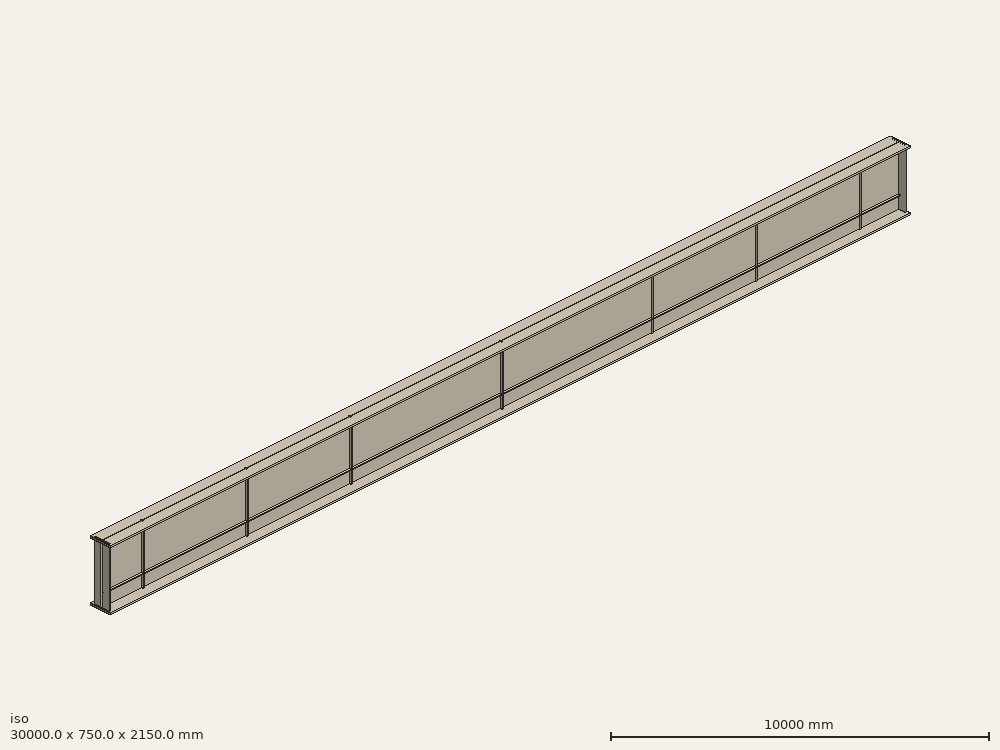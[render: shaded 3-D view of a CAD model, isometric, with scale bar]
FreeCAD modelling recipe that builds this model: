
FCSTD DOCUMENT  (FreeCAD 0.21R33694 (Git))
Label: Plate_girder_EC3
License: All rights reserved
LicenseURL: http://en.wikipedia.org/wiki/All_rights_reserved
objects: Sketcher::SketchObject×13, Part::Extrusion×13, Fem::ConstraintForce×5, Part::FeaturePython×2, Fem::ConstraintDisplacement×2, Fem::FemSolverObjectPython×1, App::MaterialObjectPython×1, Fem::FemAnalysis×1, Fem::FemMeshObjectPython×1
note: 28 computed .brp shape members not serialized (recipe doc carries the construction recipe); baked Part::Feature solids carry a one-line shape summary decoded from their .brp

FEATURE [Fem::FemSolverObjectPython] SolverCcxTools  # FEM object (typed FeaturePython)
  AnalysisType = 0
  BeamShellResultOutput3D = false
  BucklingFactors = 1
  EigenmodeHighLimit = 1000000
  EigenmodeLowLimit = 0
  EigenmodesCount = 10
  GeometricalNonlinearity = 0
  IterationsControlParameterCutb = 0.25,0.5,0.75,0.85,,,1.5,
  IterationsControlParameterIter = 4,8,9,200,10,400,,200,,
  IterationsControlParameterTimeUse = false
  IterationsThermoMechMaximum = 2000
  IterationsUserDefinedIncrementations = false
  IterationsUserDefinedTimeStepLength = false
  MaterialNonlinearity = 0
  MatrixSolverType = 0
  SplitInputWriter = false
  ThermoMechSteadyState = true
  TimeEnd = 1
  TimeInitialStep = 0.01
FEATURE [App::MaterialObjectPython] MaterialSolid  # material (typed FeaturePython)
  Category = 0
  Material = AuthorAndLicense=(c) 2014 M. Münch - GNU Lesser General Public License (LGPL),CardName=Steel-St-E-315,Density=7800 kg/m^3,Father=Metal,+13 more (map truncated)
FEATURE [Sketcher::SketchObject] Sketch001  label="end stiffener"
  FullyConstrained = true
  Placement = pos=(0,0,0) rot=(0.57735,0.57735,0.57735;2.0944rad)
  sketch-geometry (4):
    g0: LineSegment StartX=87.5 StartY=2100 StartZ=0 EndX=662.5 EndY=2100 EndZ=0
    g1: LineSegment StartX=662.5 StartY=2100 StartZ=0 EndX=662.5 EndY=0 EndZ=0
    g2: LineSegment StartX=662.5 StartY=0 StartZ=0 EndX=87.5 EndY=0 EndZ=0
    g3: LineSegment StartX=87.5 StartY=0 StartZ=0 EndX=87.5 EndY=2100 EndZ=0
  constraints (12):
    c: Coincident(g0,g1)
    c: Coincident(g1,g2)
    c: Coincident(g2,g3)
    c: Coincident(g3,g0)
    c: Horizontal(g0)
    c: Horizontal(g2)
    c: Vertical(g1)
    c: Vertical(g3)
    c: DistanceY(g1,g1) = 2100
    c: PointOnObject(g2,g-1)
    c: DistanceX(g2,g2) = 575
    c: DistanceX(g-1,g2) = 87.5
FEATURE [Sketcher::SketchObject] Sketch002  label="stiffener"
  FullyConstrained = true
  Placement = pos=(0,0,0) rot=(0.57735,0.57735,0.57735;2.0944rad)
  sketch-geometry (4):
    g0: LineSegment StartX=287.5 StartY=2100 StartZ=0 EndX=462.5 EndY=2100 EndZ=0
    g1: LineSegment StartX=462.5 StartY=2100 StartZ=0 EndX=462.5 EndY=0 EndZ=0
    g2: LineSegment StartX=462.5 StartY=0 StartZ=0 EndX=287.5 EndY=0 EndZ=0
    g3: LineSegment StartX=287.5 StartY=0 StartZ=0 EndX=287.5 EndY=2100 EndZ=0
  constraints (12):
    c: Coincident(g0,g1)
    c: Coincident(g1,g2)
    c: Coincident(g2,g3)
    c: Coincident(g3,g0)
    c: Horizontal(g0)
    c: Horizontal(g2)
    c: Vertical(g1)
    c: Vertical(g3)
    c: DistanceY(g1,g1) = 2100
    c: PointOnObject(g2,g-1)
    c: DistanceX(g0,g0) = 175
    c: DistanceX(g-1,g2) = 287.5
FEATURE [Sketcher::SketchObject] Sketch003
  FullyConstrained = true
  sketch-geometry (4):
    g0: LineSegment StartX=0 StartY=462.5 StartZ=0 EndX=175 EndY=462.5 EndZ=0
    g1: LineSegment StartX=175 StartY=462.5 StartZ=0 EndX=175 EndY=287.5 EndZ=0
    g2: LineSegment StartX=175 StartY=287.5 StartZ=0 EndX=0 EndY=287.5 EndZ=0
    g3: LineSegment StartX=0 StartY=287.5 StartZ=0 EndX=0 EndY=462.5 EndZ=0
  constraints (12):
    c: Coincident(g0,g1)
    c: Coincident(g1,g2)
    c: Coincident(g2,g3)
    c: Coincident(g3,g0)
    c: Horizontal(g0)
    c: Horizontal(g2)
    c: Vertical(g1)
    c: Vertical(g3)
    c: DistanceX(g0,g0) = 175
    c: DistanceY(g1,g1) = 175
    c: PointOnObject(g2,g-2)
    c: DistanceY(g-1,g2) = 287.5
FEATURE [Part::Extrusion] Extrude001  label="load pad"
  Base = -> Sketch003
  Dir = (0,0,1)
  DirMode = 2
  FaceMakerClass = Part::FaceMakerBullseye
  LengthFwd = 0
  LengthRev = 50
  Placement = pos=(9262.5,0,0) rot=(0,0,1;0rad)
  Solid = true
  Symmetric = false
FEATURE [Part::Extrusion] Extrude002  label="stiffener001"
  Base = -> Sketch002
  Dir = (1,0,0)
  DirMode = 2
  FaceMakerClass = Part::FaceMakerBullseye
  LengthFwd = 15
  LengthRev = 0
  Placement = pos=(1542.5,0,0) rot=(0,0,1;0rad)
  Solid = true
  Symmetric = false
FEATURE [Part::Extrusion] Extrude003  label="end stiffener001"
  Base = -> Sketch001
  Dir = (1,0,0)
  DirMode = 2
  FaceMakerClass = Part::FaceMakerBullseye
  LengthFwd = 24
  LengthRev = 0
  Placement = pos=(50,0,0) rot=(0,0,1;0rad)
  Solid = true
  Symmetric = false
FEATURE [Sketcher::SketchObject] Sketch004  label="end stiffener003"
  FullyConstrained = true
  Placement = pos=(0,0,0) rot=(0.57735,0.57735,0.57735;2.0944rad)
  sketch-geometry (4):
    g0: LineSegment StartX=87.5 StartY=2100 StartZ=0 EndX=662.5 EndY=2100 EndZ=0
    g1: LineSegment StartX=662.5 StartY=2100 StartZ=0 EndX=662.5 EndY=0 EndZ=0
    g2: LineSegment StartX=662.5 StartY=0 StartZ=0 EndX=87.5 EndY=0 EndZ=0
    g3: LineSegment StartX=87.5 StartY=0 StartZ=0 EndX=87.5 EndY=2100 EndZ=0
  constraints (12):
    c: Coincident(g0,g1)
    c: Coincident(g1,g2)
    c: Coincident(g2,g3)
    c: Coincident(g3,g0)
    c: Horizontal(g0)
    c: Horizontal(g2)
    c: Vertical(g1)
    c: Vertical(g3)
    c: DistanceY(g1,g1) = 2100
    c: PointOnObject(g2,g-1)
    c: DistanceX(g2,g2) = 575
    c: DistanceX(g-1,g2) = 87.5
FEATURE [Part::Extrusion] Extrude004  label="end stiffener002"
  Base = -> Sketch004
  Dir = (1,0,0)
  DirMode = 2
  FaceMakerClass = Part::FaceMakerBullseye
  LengthFwd = 24
  LengthRev = 0
  Placement = pos=(29926,0,0) rot=(0,0,1;0rad)
  Solid = true
  Symmetric = false
FEATURE [Sketcher::SketchObject] Sketch005  label="stiffener003"
  FullyConstrained = true
  Placement = pos=(0,0,0) rot=(0.57735,0.57735,0.57735;2.0944rad)
  sketch-geometry (4):
    g0: LineSegment StartX=287.5 StartY=2100 StartZ=0 EndX=462.5 EndY=2100 EndZ=0
    g1: LineSegment StartX=462.5 StartY=2100 StartZ=0 EndX=462.5 EndY=0 EndZ=0
    g2: LineSegment StartX=462.5 StartY=0 StartZ=0 EndX=287.5 EndY=0 EndZ=0
    g3: LineSegment StartX=287.5 StartY=0 StartZ=0 EndX=287.5 EndY=2100 EndZ=0
  constraints (12):
    c: Coincident(g0,g1)
    c: Coincident(g1,g2)
    c: Coincident(g2,g3)
    c: Coincident(g3,g0)
    c: Horizontal(g0)
    c: Horizontal(g2)
    c: Vertical(g1)
    c: Vertical(g3)
    c: DistanceY(g1,g1) = 2100
    c: PointOnObject(g2,g-1)
    c: DistanceX(g0,g0) = 175
    c: DistanceX(g-1,g2) = 287.5
FEATURE [Part::Extrusion] Extrude005  label="stiffener002"
  Base = -> Sketch005
  Dir = (1,0,0)
  DirMode = 2
  FaceMakerClass = Part::FaceMakerBullseye
  LengthFwd = 15
  LengthRev = 0
  Placement = pos=(5442.5,0,0) rot=(0,0,1;0rad)
  Solid = true
  Symmetric = false
FEATURE [Sketcher::SketchObject] Sketch006  label="stiffener005"
  FullyConstrained = true
  Placement = pos=(0,0,0) rot=(0.57735,0.57735,0.57735;2.0944rad)
  sketch-geometry (4):
    g0: LineSegment StartX=287.5 StartY=2100 StartZ=0 EndX=462.5 EndY=2100 EndZ=0
    g1: LineSegment StartX=462.5 StartY=2100 StartZ=0 EndX=462.5 EndY=0 EndZ=0
    g2: LineSegment StartX=462.5 StartY=0 StartZ=0 EndX=287.5 EndY=0 EndZ=0
    g3: LineSegment StartX=287.5 StartY=0 StartZ=0 EndX=287.5 EndY=2100 EndZ=0
  constraints (12):
    c: Coincident(g0,g1)
    c: Coincident(g1,g2)
    c: Coincident(g2,g3)
    c: Coincident(g3,g0)
    c: Horizontal(g0)
    c: Horizontal(g2)
    c: Vertical(g1)
    c: Vertical(g3)
    c: DistanceY(g1,g1) = 2100
    c: PointOnObject(g2,g-1)
    c: DistanceX(g0,g0) = 175
    c: DistanceX(g-1,g2) = 287.5
FEATURE [Part::Extrusion] Extrude006  label="stiffener004"
  Base = -> Sketch006
  Dir = (1,0,0)
  DirMode = 2
  FaceMakerClass = Part::FaceMakerBullseye
  LengthFwd = 15
  LengthRev = 0
  Placement = pos=(9342.5,0,0) rot=(0,0,1;0rad)
  Solid = true
  Symmetric = false
FEATURE [Sketcher::SketchObject] Sketch007  label="stiffener007"
  FullyConstrained = true
  Placement = pos=(0,0,0) rot=(0.57735,0.57735,0.57735;2.0944rad)
  sketch-geometry (4):
    g0: LineSegment StartX=287.5 StartY=2100 StartZ=0 EndX=462.5 EndY=2100 EndZ=0
    g1: LineSegment StartX=462.5 StartY=2100 StartZ=0 EndX=462.5 EndY=0 EndZ=0
    g2: LineSegment StartX=462.5 StartY=0 StartZ=0 EndX=287.5 EndY=0 EndZ=0
    g3: LineSegment StartX=287.5 StartY=0 StartZ=0 EndX=287.5 EndY=2100 EndZ=0
  constraints (12):
    c: Coincident(g0,g1)
    c: Coincident(g1,g2)
    c: Coincident(g2,g3)
    c: Coincident(g3,g0)
    c: Horizontal(g0)
    c: Horizontal(g2)
    c: Vertical(g1)
    c: Vertical(g3)
    c: DistanceY(g1,g1) = 2100
    c: PointOnObject(g2,g-1)
    c: DistanceX(g0,g0) = 175
    c: DistanceX(g-1,g2) = 287.5
FEATURE [Part::Extrusion] Extrude007  label="stiffener006"
  Base = -> Sketch007
  Dir = (1,0,0)
  DirMode = 2
  FaceMakerClass = Part::FaceMakerBullseye
  LengthFwd = 15
  LengthRev = 0
  Placement = pos=(14992.5,0,0) rot=(0,0,1;0rad)
  Solid = true
  Symmetric = false
FEATURE [Sketcher::SketchObject] Sketch008  label="stiffener009"
  FullyConstrained = true
  Placement = pos=(0,0,0) rot=(0.57735,0.57735,0.57735;2.0944rad)
  sketch-geometry (4):
    g0: LineSegment StartX=287.5 StartY=2100 StartZ=0 EndX=462.5 EndY=2100 EndZ=0
    g1: LineSegment StartX=462.5 StartY=2100 StartZ=0 EndX=462.5 EndY=0 EndZ=0
    g2: LineSegment StartX=462.5 StartY=0 StartZ=0 EndX=287.5 EndY=0 EndZ=0
    g3: LineSegment StartX=287.5 StartY=0 StartZ=0 EndX=287.5 EndY=2100 EndZ=0
  constraints (12):
    c: Coincident(g0,g1)
    c: Coincident(g1,g2)
    c: Coincident(g2,g3)
    c: Coincident(g3,g0)
    c: Horizontal(g0)
    c: Horizontal(g2)
    c: Vertical(g1)
    c: Vertical(g3)
    c: DistanceY(g1,g1) = 2100
    c: PointOnObject(g2,g-1)
    c: DistanceX(g0,g0) = 175
    c: DistanceX(g-1,g2) = 287.5
FEATURE [Part::Extrusion] Extrude008  label="stiffener008"
  Base = -> Sketch008
  Dir = (1,0,0)
  DirMode = 2
  FaceMakerClass = Part::FaceMakerBullseye
  LengthFwd = 15
  LengthRev = 0
  Placement = pos=(20642.5,0,0) rot=(0,0,1;0rad)
  Solid = true
  Symmetric = false
FEATURE [Sketcher::SketchObject] Sketch009  label="stiffener011"
  FullyConstrained = true
  Placement = pos=(0,0,0) rot=(0.57735,0.57735,0.57735;2.0944rad)
  sketch-geometry (4):
    g0: LineSegment StartX=287.5 StartY=2100 StartZ=0 EndX=462.5 EndY=2100 EndZ=0
    g1: LineSegment StartX=462.5 StartY=2100 StartZ=0 EndX=462.5 EndY=0 EndZ=0
    g2: LineSegment StartX=462.5 StartY=0 StartZ=0 EndX=287.5 EndY=0 EndZ=0
    g3: LineSegment StartX=287.5 StartY=0 StartZ=0 EndX=287.5 EndY=2100 EndZ=0
  constraints (12):
    c: Coincident(g0,g1)
    c: Coincident(g1,g2)
    c: Coincident(g2,g3)
    c: Coincident(g3,g0)
    c: Horizontal(g0)
    c: Horizontal(g2)
    c: Vertical(g1)
    c: Vertical(g3)
    c: DistanceY(g1,g1) = 2100
    c: PointOnObject(g2,g-1)
    c: DistanceX(g0,g0) = 175
    c: DistanceX(g-1,g2) = 287.5
FEATURE [Part::Extrusion] Extrude009  label="stiffener010"
  Base = -> Sketch009
  Dir = (1,0,0)
  DirMode = 2
  FaceMakerClass = Part::FaceMakerBullseye
  LengthFwd = 15
  LengthRev = 0
  Placement = pos=(24542.5,0,0) rot=(0,0,1;0rad)
  Solid = true
  Symmetric = false
FEATURE [Sketcher::SketchObject] Sketch010  label="stiffener013"
  FullyConstrained = true
  Placement = pos=(0,0,0) rot=(0.57735,0.57735,0.57735;2.0944rad)
  sketch-geometry (4):
    g0: LineSegment StartX=287.5 StartY=2100 StartZ=0 EndX=462.5 EndY=2100 EndZ=0
    g1: LineSegment StartX=462.5 StartY=2100 StartZ=0 EndX=462.5 EndY=0 EndZ=0
    g2: LineSegment StartX=462.5 StartY=0 StartZ=0 EndX=287.5 EndY=0 EndZ=0
    g3: LineSegment StartX=287.5 StartY=0 StartZ=0 EndX=287.5 EndY=2100 EndZ=0
  constraints (12):
    c: Coincident(g0,g1)
    c: Coincident(g1,g2)
    c: Coincident(g2,g3)
    c: Coincident(g3,g0)
    c: Horizontal(g0)
    c: Horizontal(g2)
    c: Vertical(g1)
    c: Vertical(g3)
    c: DistanceY(g1,g1) = 2100
    c: PointOnObject(g2,g-1)
    c: DistanceX(g0,g0) = 175
    c: DistanceX(g-1,g2) = 287.5
FEATURE [Part::Extrusion] Extrude010  label="stiffener012"
  Base = -> Sketch010
  Dir = (1,0,0)
  DirMode = 2
  FaceMakerClass = Part::FaceMakerBullseye
  LengthFwd = 15
  LengthRev = 0
  Placement = pos=(28442.5,0,0) rot=(0,0,1;0rad)
  Solid = true
  Symmetric = false
FEATURE [Sketcher::SketchObject] Sketch  label="girder"
  FullyConstrained = true
  Placement = pos=(0,0,0) rot=(0.57735,0.57735,0.57735;2.0944rad)
  sketch-geometry (16):
    g0: LineSegment StartX=750 StartY=2100 StartZ=0 EndX=750 EndY=2050 EndZ=0
    g1: LineSegment StartX=750 StartY=2050 StartZ=0 EndX=382.5 EndY=2050 EndZ=0
    g2: LineSegment StartX=382.5 StartY=2050 StartZ=0 EndX=382.5 EndY=50 EndZ=0
    g3: LineSegment StartX=382.5 StartY=50 StartZ=0 EndX=750 EndY=50 EndZ=0
    g4: LineSegment StartX=750 StartY=50 StartZ=0 EndX=750 EndY=0 EndZ=0
    g5: LineSegment StartX=0 StartY=0 StartZ=0 EndX=0 EndY=50 EndZ=0
    g6: LineSegment StartX=0 StartY=50 StartZ=0 EndX=367.5 EndY=50 EndZ=0
    g7: LineSegment StartX=367.5 StartY=50 StartZ=0 EndX=367.5 EndY=2050 EndZ=0
    g8: LineSegment StartX=367.5 StartY=2050 StartZ=0 EndX=0 EndY=2050 EndZ=0
    g9: LineSegment StartX=750 StartY=2100 StartZ=0 EndX=382.5 EndY=2100 EndZ=0
    g10: LineSegment StartX=750 StartY=0 StartZ=0 EndX=382.5 EndY=0 EndZ=0
    g11: LineSegment StartX=367.5 StartY=0 StartZ=0 EndX=0 EndY=0 EndZ=0
    g12: LineSegment StartX=382.5 StartY=2100 StartZ=0 EndX=367.5 EndY=2100 EndZ=0
    g13: LineSegment StartX=0 StartY=2050 StartZ=0 EndX=0 EndY=2100 EndZ=0
    g14: LineSegment StartX=367.5 StartY=0 StartZ=0 EndX=382.5 EndY=0 EndZ=0
    g15: LineSegment StartX=0 StartY=2100 StartZ=0 EndX=367.5 EndY=2100 EndZ=0
  constraints (48):
    c: Vertical(g0)
    c: Coincident(g0,g1)
    c: Horizontal(g1)
    c: Coincident(g1,g2)
    c: Vertical(g2)
    c: Coincident(g2,g3)
    c: Horizontal(g3)
    c: Coincident(g3,g4)
    c: PointOnObject(g4,g-1)
    c: Vertical(g5)
    c: Coincident(g5,g6)
    c: Horizontal(g6)
    c: Coincident(g6,g7)
    c: Vertical(g7)
    c: Coincident(g7,g8)
    c: Horizontal(g8)
    c: Vertical(g4)
    c: DistanceY(g0,g0) = 50
    c: DistanceX(g6,g6) = 367.5
    c: DistanceX(g3,g3) = 367.5
    c: DistanceY(g4,g4) = 50
    c: DistanceY(g5,g5) = 50
    c: DistanceY(g4,g0) = 2100
    c: DistanceX(g-1,g5) = 0
    c: Coincident(g9,g0)
    c: Horizontal(g9)
    c: Coincident(g10,g4)
    c: Horizontal(g10)
    c: Coincident(g11,g5)
    c: Horizontal(g11)
    c: Coincident(g12,g9)
    c: Horizontal(g12)
    c: Coincident(g13,g8)
    c: Vertical(g13)
    c: DistanceX(g7,g1) = 15
    c: Equal(g11,g6)
    c: Equal(g10,g3)
    c: Coincident(g14,g11)
    c: Coincident(g14,g10)
    c: DistanceY(g13,g13) = 50
    c: DistanceY(g-1,g5) = 0
    c: Coincident(g15,g13)
    c: Coincident(g15,g12)
    c: Horizontal(g15)
    c: DistanceX(g15,g15) = 367.5
    c: DistanceX(g12,g12) = 15
    c: DistanceX(g9,g9) = 367.5
    c: PointOnObject(g13,g-2)
FEATURE [Part::Extrusion] Extrude
  Base = -> Sketch
  Dir = (1,0,0)
  DirMode = 2
  FaceMakerClass = Part::FaceMakerBullseye
  LengthFwd = 30000
  LengthRev = 0
  Solid = true
  Symmetric = false
FEATURE [Sketcher::SketchObject] Sketch011
  FullyConstrained = true
  sketch-geometry (4):
    g0: LineSegment StartX=0 StartY=462.5 StartZ=0 EndX=175 EndY=462.5 EndZ=0
    g1: LineSegment StartX=175 StartY=462.5 StartZ=0 EndX=175 EndY=287.5 EndZ=0
    g2: LineSegment StartX=175 StartY=287.5 StartZ=0 EndX=0 EndY=287.5 EndZ=0
    g3: LineSegment StartX=0 StartY=287.5 StartZ=0 EndX=0 EndY=462.5 EndZ=0
  constraints (12):
    c: Coincident(g0,g1)
    c: Coincident(g1,g2)
    c: Coincident(g2,g3)
    c: Coincident(g3,g0)
    c: Horizontal(g0)
    c: Horizontal(g2)
    c: Vertical(g1)
    c: Vertical(g3)
    c: DistanceX(g0,g0) = 175
    c: DistanceY(g1,g1) = 175
    c: PointOnObject(g2,g-2)
    c: DistanceY(g-1,g2) = 287.5
FEATURE [Part::Extrusion] Extrude011  label="load pad001"
  Base = -> Sketch011
  Dir = (0,0,1)
  DirMode = 2
  FaceMakerClass = Part::FaceMakerBullseye
  LengthFwd = 0
  LengthRev = 50
  Placement = pos=(20562.5,0,0) rot=(0,0,1;0rad)
  Solid = true
  Symmetric = false
FEATURE [Part::FeaturePython] BooleanFragments  # WARN: FeaturePython — macro-defined, semantics opaque (R4)
  Mode = 2
  Objects = -> [Extrude001,Extrude002,Extrude003,Extrude004,Extrude005,Extrude006,Extrude007,Extrude008,Extrude009,Extrude010,Extrude,Extrude011]
  Tolerance = 0
FEATURE [Fem::ConstraintDisplacement] ConstraintDisplacement003
  NormalDirection = (0,0,1)
  Normals = (10) [(0,0,1),(0,0,1),(0,0,1),(0,0,1),(0,0,1),(0,0,1),(0,0,1),(0,0,1),(0,0,1),(0,0,1)]
  Points = (10) [(50,87.5,2100),(50,180.833,2100),(50,274.167,2100),(50,367.5,2100),(50,367.5,2100),(50,382.5,2100),(50,382.5,2100),(50,475.833,2100),+2 more]
  References = -> [BooleanFragments]
  Scale = 18
  hasXFormula = false
  hasYFormula = false
  hasZFormula = false
  rotxFix = false
  rotxFree = true
  rotyFix = false
  rotyFree = true
  rotzFix = false
  rotzFree = true
  useFlowSurfaceForce = false
  xDisplacement = 0
  xFix = false
  xFree = false
  xRotation = 0
  yDisplacement = 0
  yFix = false
  yFree = false
  yRotation = 0
  zDisplacement = 0
  zFix = false
  zFree = false
  zRotation = 0
FEATURE [Fem::ConstraintDisplacement] ConstraintDisplacement004
  NormalDirection = (0,0,1)
  Normals = (10) [(0,0,1),(0,0,1),(0,0,1),(0,0,1),(0,0,1),(0,0,1),(0,0,1),(0,0,1),(0,0,1),(0,0,1)]
  Points = (10) [(29950,87.5,2100),(29950,180.833,2100),(29950,274.167,2100),(29950,367.5,2100),(29950,367.5,2100),(29950,382.5,2100),(29950,382.5,2100),+3 more]
  References = -> [BooleanFragments]
  Scale = 18
  hasXFormula = false
  hasYFormula = false
  hasZFormula = false
  rotxFix = false
  rotxFree = true
  rotyFix = false
  rotyFree = true
  rotzFix = false
  rotzFree = true
  useFlowSurfaceForce = false
  xDisplacement = 0
  xFix = false
  xFree = true
  xRotation = 0
  yDisplacement = 0
  yFix = false
  yFree = false
  yRotation = 0
  zDisplacement = 0
  zFix = false
  zFree = false
  zRotation = 0
FEATURE [Fem::ConstraintForce] ConstraintForce005
  DirectionVector = (0,0,-1)
  Force = 2293000
  NormalDirection = (0,0,1)
  Points = (33) [(29950,87.5,2100),(29950,180.833,2100),(29950,274.167,2100),(29950,367.5,2100),(29938,87.5,2100),(29938,180.833,2100),(29938,274.167,2100),+26 more]
  References = -> [BooleanFragments]
  Reversed = true
  Scale = 13
FEATURE [Fem::ConstraintForce] ConstraintForce006
  DirectionVector = (0,0,-1)
  Force = 2293000
  NormalDirection = (0,0,1)
  Points = (33) [(74,87.5,2100),(74,180.833,2100),(74,274.167,2100),(74,367.5,2100),(62,87.5,2100),(62,180.833,2100),(62,274.167,2100),(62,367.5,2100),(50,87.5,2100),+24 more]
  References = -> [BooleanFragments]
  Reversed = true
  Scale = 13
FEATURE [Fem::ConstraintForce] ConstraintForce007
  DirectionVector = (0,0,1)
  Force = 925000
  NormalDirection = (0,0,-1)
  Points = (16) [(9262.5,287.5,-50),(9320.83,287.5,-50),(9379.17,287.5,-50),(9437.5,287.5,-50),(9262.5,345.833,-50),(9320.83,345.833,-50),(9379.17,345.833,-50),+9 more]
  References = -> [BooleanFragments]
  Reversed = true
  Scale = 14
FEATURE [Fem::ConstraintForce] ConstraintForce008
  DirectionVector = (0,0,1)
  Force = 925000
  NormalDirection = (0,0,-1)
  Points = (16) [(20562.5,287.5,-50),(20620.8,287.5,-50),(20679.2,287.5,-50),(20737.5,287.5,-50),(20562.5,345.833,-50),(20620.8,345.833,-50),(20679.2,345.833,-50),+9 more]
  References = -> [BooleanFragments]
  Reversed = true
  Scale = 14
FEATURE [Fem::ConstraintForce] ConstraintForce009
  DirectionVector = (0,0,1)
  Force = 2736000
  NormalDirection = (0,0,-1)
  Points = (323) [(29950,382.5,0),(29950,375,0),(29950,367.5,0),(29938,382.5,0),(29938,375,0),(29938,367.5,0),(29926,382.5,0),(29926,375,0),(29926,367.5,0),+314 more]
  References = -> [BooleanFragments]
  Reversed = true
FEATURE [Fem::FemAnalysis] Analysis
  Group = -> [SolverCcxTools,MaterialSolid,ConstraintDisplacement003,ConstraintDisplacement004,ConstraintForce005,ConstraintForce006,ConstraintForce007,ConstraintForce008,ConstraintForce009]
FEATURE [Sketcher::SketchObject] Sketch012
  FullyConstrained = true
  Placement = pos=(0,0,0) rot=(0.57735,0.57735,0.57735;2.0944rad)
  sketch-geometry (4):
    g0: LineSegment StartX=287.5 StartY=520 StartZ=0 EndX=462.5 EndY=520 EndZ=0
    g1: LineSegment StartX=462.5 StartY=520 StartZ=0 EndX=462.5 EndY=500 EndZ=0
    g2: LineSegment StartX=462.5 StartY=500 StartZ=0 EndX=287.5 EndY=500 EndZ=0
    g3: LineSegment StartX=287.5 StartY=500 StartZ=0 EndX=287.5 EndY=520 EndZ=0
  constraints (12):
    c: Coincident(g0,g1)
    c: Coincident(g1,g2)
    c: Coincident(g2,g3)
    c: Coincident(g3,g0)
    c: Horizontal(g0)
    c: Horizontal(g2)
    c: Vertical(g1)
    c: Vertical(g3)
    c: DistanceX(g2,g2) = 175
    c: DistanceY(g1,g1) = 20
    c: DistanceY(g-1,g2) = 500
    c: DistanceX(g-1,g2) = 287.5
FEATURE [Part::Extrusion] Extrude012
  Base = -> Sketch012
  Dir = (1,0,0)
  DirMode = 2
  FaceMakerClass = Part::FaceMakerBullseye
  LengthFwd = 29900
  LengthRev = 0
  Placement = pos=(50,0,0) rot=(0,0,1;0rad)
  Solid = true
  Symmetric = false
FEATURE [Part::FeaturePython] BooleanFragments001  # WARN: FeaturePython — macro-defined, semantics opaque (R4)
  Mode = 2
  Objects = -> [BooleanFragments,Extrude012]
  Tolerance = 0
FEATURE [Fem::FemMeshObjectPython] FEMMeshGmsh  # FEM object (typed FeaturePython)
  Algorithm2D = 0
  Algorithm3D = 0
  CharacteristicLengthMax = 200
  CharacteristicLengthMin = 0
  CoherenceMesh = true
  ElementDimension = 0
  ElementOrder = 1
  GeometryTolerance = 1e-06
  GroupsOfNodes = false
  HighOrderOptimize = 0
  MeshSizeFromCurvature = 12
  OptimizeNetgen = false
  OptimizeStd = true
  Part = -> BooleanFragments001
  RecombinationAlgorithm = 0
  Recombine3DAll = false
  RecombineAll = false
  SecondOrderLinear = false
